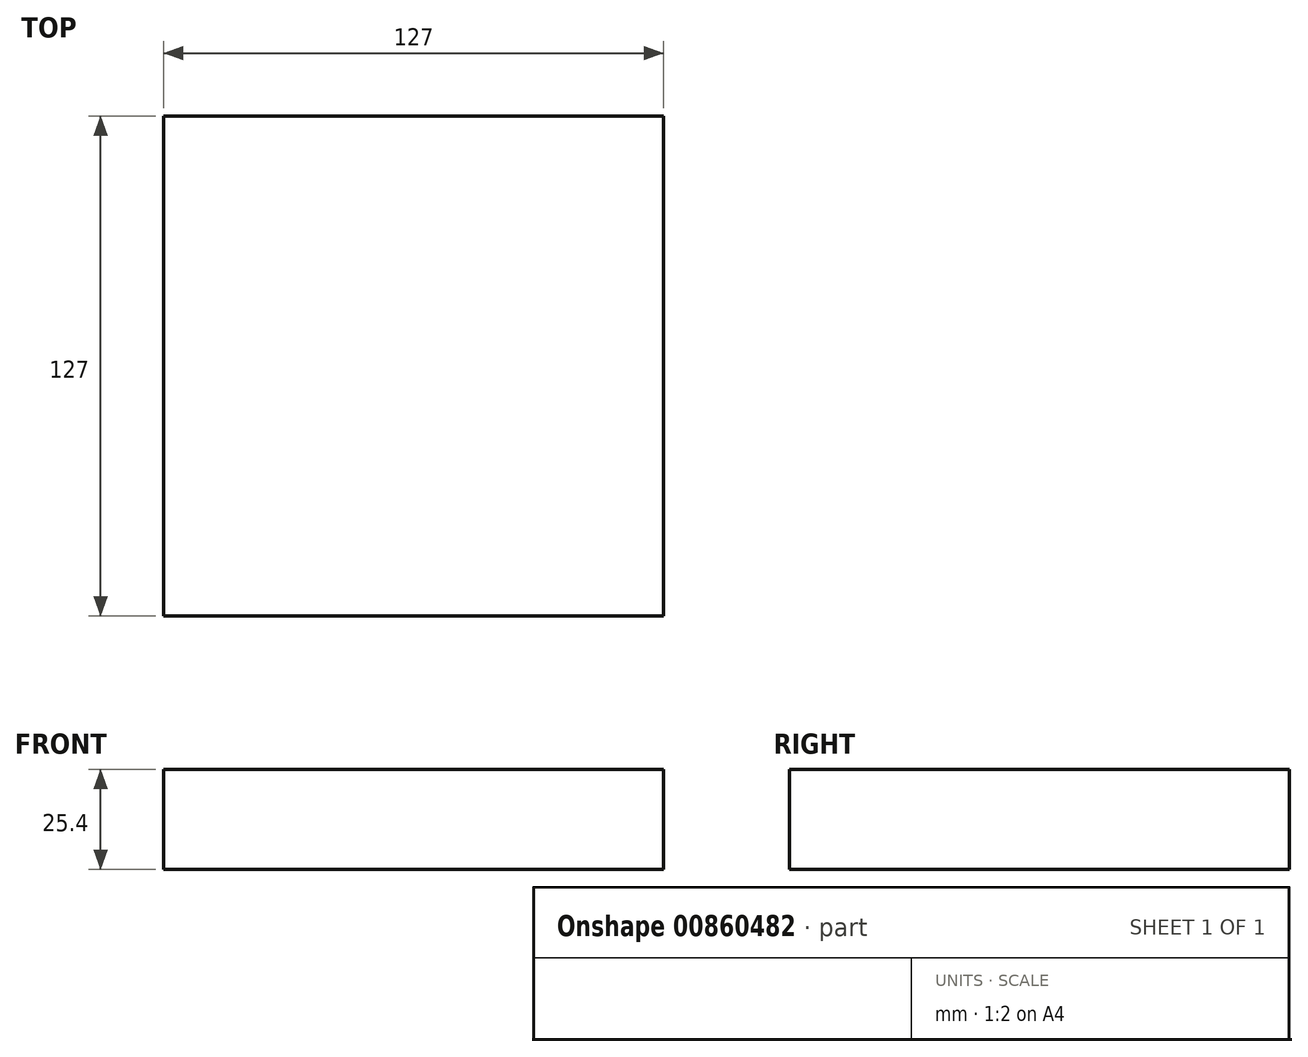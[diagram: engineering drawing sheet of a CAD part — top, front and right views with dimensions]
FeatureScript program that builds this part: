
annotation { "Feature Type Name" : "Feature", "Feature Type Description" : "" }
export const myFeature = defineFeature(function(context is Context, id is Id, definition is map)
    precondition{}
    {
        {
            var Q0;
            Q0=qCreatedBy(makeId("Top.planeOp"),FACE);
            var sketch = newSketch(context, id + "F0", { "sketchPlane" : qUnion([Q0])});
            skLineSegment(sketch, "E0.bottom", {"start": v(63.5, 63.5) * mm, "end": v(-63.5, 63.5) * mm});
            skLineSegment(sketch, "E0.top", {"start": v(63.5, -63.5) * mm, "end": v(-63.5, -63.5) * mm});
            skLineSegment(sketch, "E0.left", {"start": v(63.5, 63.5) * mm, "end": v(63.5, -63.5) * mm});
            skLineSegment(sketch, "E0.right", {"start": v(-63.5, 63.5) * mm, "end": v(-63.5, -63.5) * mm});
            skPoint(sketch, "E0.middle", {"position": v(0, 0) * mm});
            skSolve(sketch);
        }
        {
            var Q0;
            Q0=makeQuery(id+"F0.imprint","IMPRINT",FACE,{"disambiguationData":[TD([[makeQuery(id+"F0.imprint","IMPRINT",EDGE,{"derivedFrom":sQuery(id+"F0.wireOp",EDGE,"E0.bottom")}),1.0]])]});
            extrude(context, id + "F1", {"entities" : qUnion([Q0]), "depth" : 25.4 * mm, "offsetDistance" : 25.4 * mm});
        }
    });
